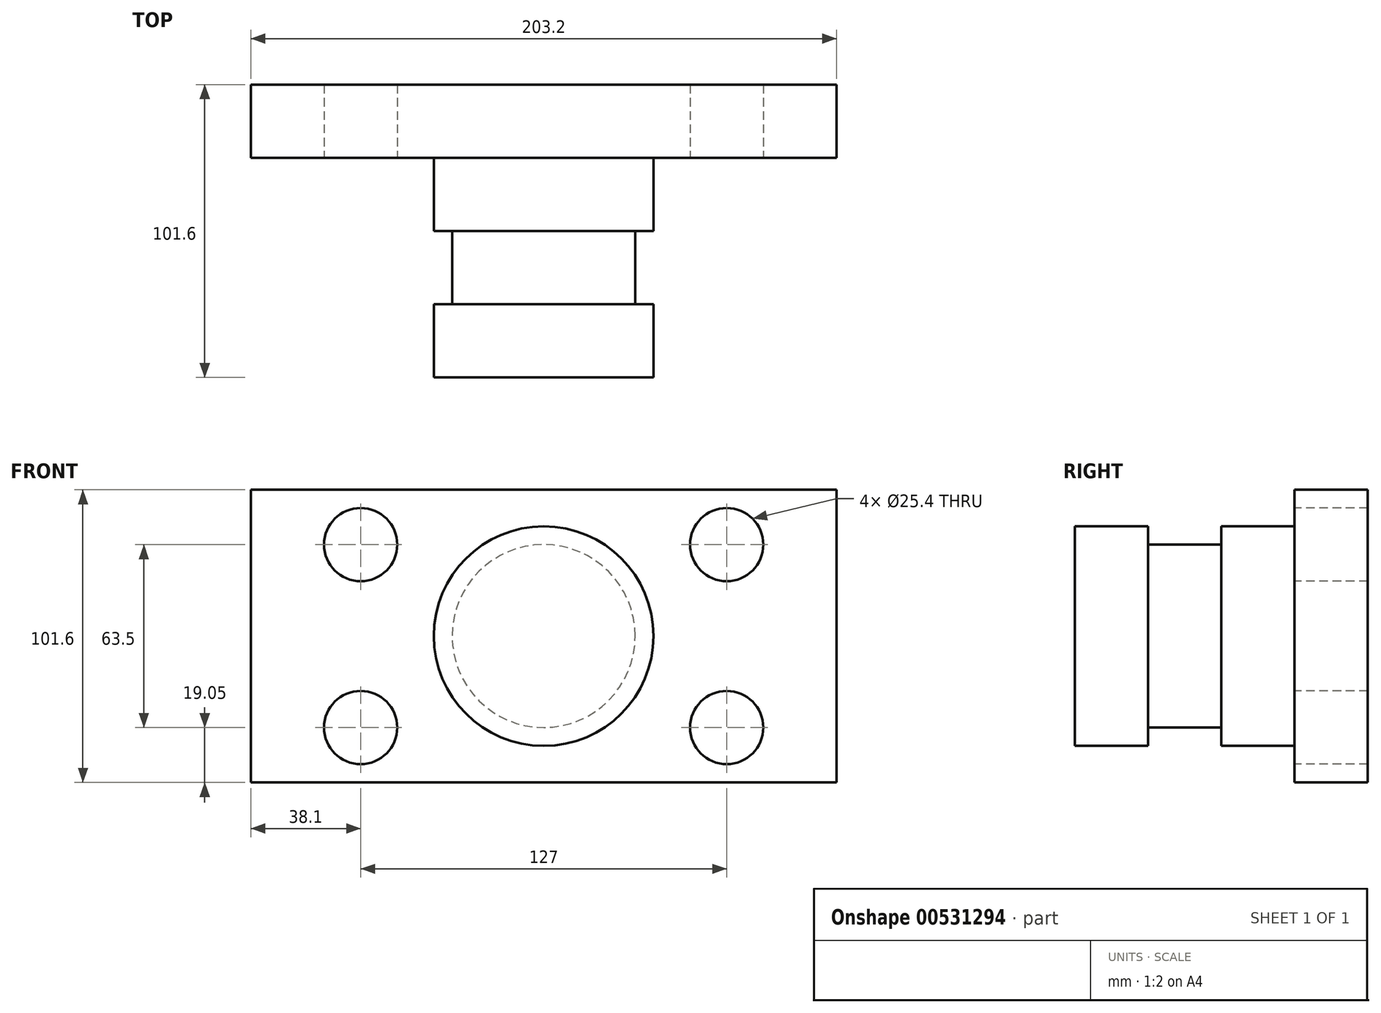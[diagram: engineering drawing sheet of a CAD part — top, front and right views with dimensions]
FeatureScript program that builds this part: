
annotation { "Feature Type Name" : "Feature", "Feature Type Description" : "" }
export const myFeature = defineFeature(function(context is Context, id is Id, definition is map)
    precondition{}
    {
        {
            var Q0;
            Q0=qCreatedBy(makeId("Front.planeOp"),FACE);
            var sketch = newSketch(context, id + "F0", { "sketchPlane" : qUnion([Q0])});
            skLineSegment(sketch, "E0.bottom", {"start": v(-101.6, 50.8) * mm, "end": v(101.6, 50.8) * mm});
            skLineSegment(sketch, "E0.top", {"start": v(-101.6, -50.8) * mm, "end": v(101.6, -50.8) * mm});
            skLineSegment(sketch, "E0.left", {"start": v(-101.6, 50.8) * mm, "end": v(-101.6, -50.8) * mm});
            skLineSegment(sketch, "E0.right", {"start": v(101.6, 50.8) * mm, "end": v(101.6, -50.8) * mm});
            skPoint(sketch, "E0.middle", {"position": v(0, 0) * mm});
            skSolve(sketch);
        }
        {
            var Q0;
            Q0=makeQuery(id+"F0.imprint","IMPRINT",FACE,{"disambiguationData":[TD([[makeQuery(id+"F0.imprint","IMPRINT",EDGE,{"derivedFrom":sQuery(id+"F0.wireOp",EDGE,"E0.bottom")}),-1.0]])]});
            extrude(context, id + "F1", {"entities" : qUnion([Q0]), "depth" : 25.4 * mm, "offsetDistance" : 25.4 * mm});
        }
        {
            var Q0;
            Q0=makeQuery(id+"F1.opExtrude","CAP_FACE",FACE,{"disambiguationData":[OSD([sQuery(id+"F0.wireOp",EDGE,"E0.bottom"),sQuery(id+"F0.wireOp",EDGE,"E0.top"),sQuery(id+"F0.wireOp",EDGE,"E0.left"),sQuery(id+"F0.wireOp",EDGE,"E0.right")])],"isStart":false});
            var sketch = newSketch(context, id + "F2", { "sketchPlane" : qUnion([Q0])});
            skCircle(sketch, "E1", {"center": v(-63.5, 31.75) * mm, "radius": 12.7 * mm});
            skCircle(sketch, "E2", {"center": v(63.5, 31.75) * mm, "radius": 12.7 * mm});
            skCircle(sketch, "E3", {"center": v(63.5, -31.75) * mm, "radius": 12.7 * mm});
            skCircle(sketch, "E4", {"center": v(-63.5, -31.75) * mm, "radius": 12.7 * mm});
            skSolve(sketch);
        }
        {
            var Q0;
            Q0=sQuery(id+"F2.wireOp",VERTEX,"E1.center");
            var Q1;
            Q1=sQuery(id+"F2.wireOp",VERTEX,"E4.center");
            var Q2;
            Q2=sQuery(id+"F2.wireOp",VERTEX,"E3.center");
            var Q3;
            Q3=sQuery(id+"F2.wireOp",VERTEX,"E2.center");
            var Q4;
            Q4=makeQuery(id+"F1.opExtrude","SWEPT_BODY",BODY,{"disambiguationData":[OSD([sQuery(id+"F0.wireOp",EDGE,"E0.bottom"),sQuery(id+"F0.wireOp",EDGE,"E0.top"),sQuery(id+"F0.wireOp",EDGE,"E0.left"),sQuery(id+"F0.wireOp",EDGE,"E0.right")])]});
            hole(context, id + "F3", {"style" : HoleStyle.SIMPLE, "endStyle" : HoleEndStyle.THROUGH, "holeDiameter" : 25.4 * mm, "isTappedThrough" : true, "tappedDepth" : 12.7 * mm, "tapClearance" : 3, "locations" : qUnion([Q0, Q1, Q2, Q3]), "scope" : qUnion([Q4])});
        }
        {
            var Q0;
            Q0=makeQuery(id+"F1.opExtrude","CAP_FACE",FACE,{"disambiguationData":[OSD([sQuery(id+"F0.wireOp",EDGE,"E0.bottom"),sQuery(id+"F0.wireOp",EDGE,"E0.top"),sQuery(id+"F0.wireOp",EDGE,"E0.left"),sQuery(id+"F0.wireOp",EDGE,"E0.right")])],"isStart":false});
            var sketch = newSketch(context, id + "F4", { "sketchPlane" : qUnion([Q0])});
            skCircle(sketch, "E5", {"center": v(0, 0) * mm, "radius": 38.1 * mm});
            skSolve(sketch);
        }
        {
            var Q0;
            Q0=makeQuery(id+"F4.imprint","IMPRINT",FACE,{"disambiguationData":[TD([[makeQuery(id+"F4.imprint","IMPRINT",EDGE,{"derivedFrom":sQuery(id+"F4.wireOp",EDGE,"E5")}),1.0]])]});
            extrude(context, id + "F5", {"entities" : qUnion([Q0]), "operationType" : NewBodyOperationType.ADD, "depth" : 25.4 * mm, "offsetDistance" : 25.4 * mm});
        }
        {
            var Q0;
            Q0=makeQuery(id+"F5.opExtrude","CAP_FACE",FACE,{"disambiguationData":[OSD([sQuery(id+"F4.wireOp",EDGE,"E5")])],"isStart":false});
            var sketch = newSketch(context, id + "F6", { "sketchPlane" : qUnion([Q0])});
            skCircle(sketch, "E6", {"center": v(0, 0) * mm, "radius": 31.75 * mm});
            skSolve(sketch);
        }
        {
            var Q0;
            Q0=makeQuery(id+"F6.imprint","IMPRINT",FACE,{"disambiguationData":[TD([[makeQuery(id+"F6.imprint","IMPRINT",EDGE,{"derivedFrom":sQuery(id+"F6.wireOp",EDGE,"E6")}),1.0]])]});
            extrude(context, id + "F7", {"entities" : qUnion([Q0]), "operationType" : NewBodyOperationType.ADD, "depth" : 25.4 * mm, "offsetDistance" : 25.4 * mm});
        }
        {
            var Q0;
            Q0=makeQuery(id+"F7.opExtrude","CAP_FACE",FACE,{"disambiguationData":[OSD([sQuery(id+"F6.wireOp",EDGE,"E6")])],"isStart":false});
            var sketch = newSketch(context, id + "F8", { "sketchPlane" : qUnion([Q0])});
            skCircle(sketch, "E7", {"center": v(0, 0) * mm, "radius": 38.1 * mm});
            skSolve(sketch);
        }
        {
            var Q0;
            Q0 = qSketchRegion(id + "F8", true);
            extrude(context, id + "F9", {"entities" : qUnion([Q0]), "operationType" : NewBodyOperationType.ADD, "depth" : 25.4 * mm, "offsetDistance" : 25.4 * mm});
        }
    });
